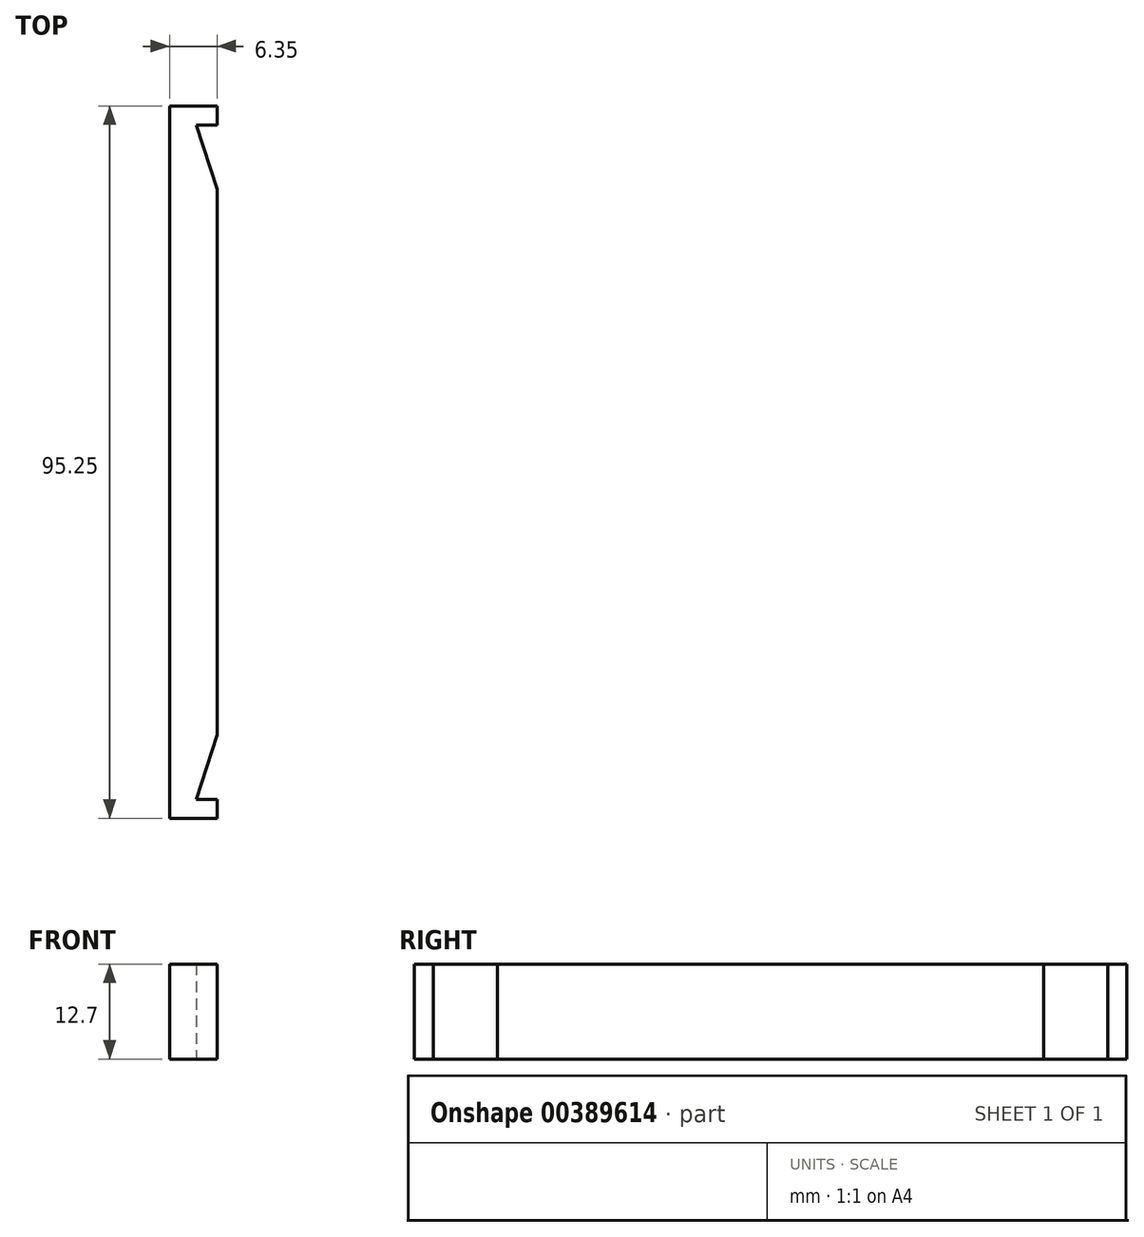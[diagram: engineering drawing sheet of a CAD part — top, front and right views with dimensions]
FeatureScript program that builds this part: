
annotation { "Feature Type Name" : "Feature", "Feature Type Description" : "" }
export const myFeature = defineFeature(function(context is Context, id is Id, definition is map)
    precondition{}
    {
        {
            var Q0;
            Q0=qCreatedBy(makeId("Top.planeOp"),FACE);
            var sketch = newSketch(context, id + "F0", { "sketchPlane" : qUnion([Q0])});
            skLineSegment(sketch, "E0", {"start": v(0, 0) * mm, "end": v(0, 95.25) * mm});
            skLineSegment(sketch, "E1", {"start": v(0, 95.25) * mm, "end": v(6.35, 95.25) * mm});
            skLineSegment(sketch, "E2", {"start": v(6.35, 95.25) * mm, "end": v(6.35, 92.71) * mm});
            skLineSegment(sketch, "E3", {"start": v(6.35, 92.71) * mm, "end": v(3.56, 92.71) * mm});
            skLineSegment(sketch, "E4", {"start": v(3.56, 92.71) * mm, "end": v(6.35, 84.13) * mm});
            skLineSegment(sketch, "E5", {"start": v(6.35, 84.13) * mm, "end": v(6.35, 11.12) * mm});
            skLineSegment(sketch, "E6", {"start": v(6.35, 11.12) * mm, "end": v(3.56, 2.54) * mm});
            skLineSegment(sketch, "E7", {"start": v(3.56, 2.54) * mm, "end": v(6.35, 2.54) * mm});
            skLineSegment(sketch, "E8", {"start": v(6.35, 2.54) * mm, "end": v(6.35, 0) * mm});
            skLineSegment(sketch, "E9", {"start": v(6.35, 0) * mm, "end": v(0, 0) * mm});
            skSolve(sketch);
        }
        {
            var Q0;
            Q0 = qSketchRegion(id + "F0", true);
            extrude(context, id + "F1", {"entities" : qUnion([Q0]), "depth" : 12.7 * mm});
        }
    });
